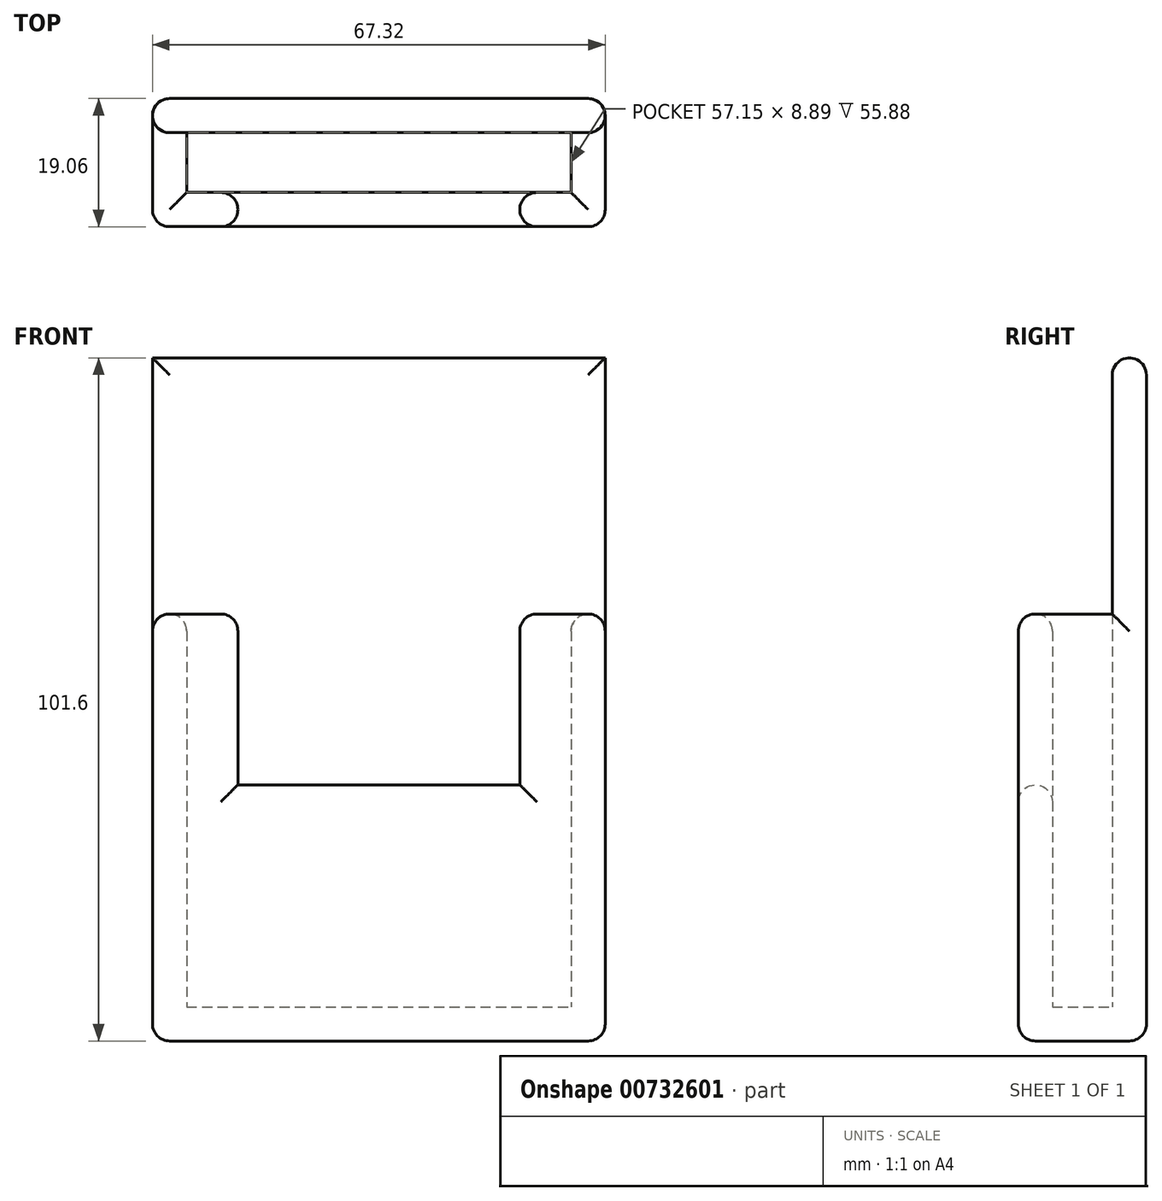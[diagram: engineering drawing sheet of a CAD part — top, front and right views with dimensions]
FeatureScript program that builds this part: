
annotation { "Feature Type Name" : "Feature", "Feature Type Description" : "" }
export const myFeature = defineFeature(function(context is Context, id is Id, definition is map)
    precondition{}
    {
        {
            var Q0;
            Q0=qCreatedBy(makeId("Top.planeOp"),FACE);
            var sketch = newSketch(context, id + "F0", { "sketchPlane" : qUnion([Q0])});
            skLineSegment(sketch, "E0.bottom", {"start": v(-33.66, 9.53) * mm, "end": v(33.66, 9.53) * mm});
            skLineSegment(sketch, "E0.top", {"start": v(-33.66, -9.53) * mm, "end": v(33.66, -9.53) * mm});
            skLineSegment(sketch, "E0.left", {"start": v(-33.66, 9.53) * mm, "end": v(-33.66, -9.53) * mm});
            skLineSegment(sketch, "E0.right", {"start": v(33.66, 9.53) * mm, "end": v(33.66, -9.53) * mm});
            skPoint(sketch, "E0.middle", {"position": v(0, 0) * mm});
            skLineSegment(sketch, "E1.0", {"start": v(-28.58, 4.45) * mm, "end": v(28.58, 4.45) * mm});
            skLineSegment(sketch, "E1.1", {"start": v(-28.58, 4.45) * mm, "end": v(-28.58, -4.45) * mm});
            skLineSegment(sketch, "E1.2", {"start": v(-28.58, -4.45) * mm, "end": v(28.58, -4.45) * mm});
            skLineSegment(sketch, "E1.3", {"start": v(28.58, 4.44) * mm, "end": v(28.58, -4.45) * mm});
            skLineSegment(sketch, "E2", {"start": v(-20.96, -4.45) * mm, "end": v(-20.96, -9.53) * mm});
            skLineSegment(sketch, "E3", {"start": v(20.96, -4.45) * mm, "end": v(20.96, -9.53) * mm});
            skLineSegment(sketch, "E4", {"start": v(-28.58, 4.45) * mm, "end": v(-33.66, 4.45) * mm});
            skLineSegment(sketch, "E5", {"start": v(28.58, 4.44) * mm, "end": v(33.66, 4.44) * mm});
            skSolve(sketch);
        }
        {
            var Q0;
            Q0 = qSketchRegion(id + "F0", true);
            var Q1;
            Q1=makeQuery(id+"F0.imprint","IMPRINT",FACE,{"disambiguationData":[TD([[makeQuery(id+"F0.imprint","IMPRINT",EDGE,{"derivedFrom":sQuery(id+"F0.wireOp",EDGE,"E1.0")}),-1.0]])]});
            extrude(context, id + "F1", {"entities" : qUnion([Q0, Q1]), "depth" : 5.08 * mm, "offsetDistance" : 25.4 * mm});
        }
        {
            var Q0;
            {var subQ1=sQuery(id+"F0.wireOp",EDGE,"E0.bottom");Q0=makeQuery(id+"F0.imprint","IMPRINT",FACE,{"disambiguationData":[TD([[makeQuery(id+"F0.imprint","IMPRINT",EDGE,{"derivedFrom":subQ1}),-1.0]])]});}
            extrude(context, id + "F2", {"entities" : qUnion([Q0]), "operationType" : NewBodyOperationType.ADD, "depth" : 101.6 * mm, "offsetDistance" : 25.4 * mm});
        }
        {
            var Q0;
            {var subQ0=sQuery(id+"F0.wireOp",EDGE,"E1.1");Q0=makeQuery(id+"F0.imprint","IMPRINT",FACE,{"disambiguationData":[TD([[makeQuery(id+"F0.imprint","IMPRINT",EDGE,{"derivedFrom":subQ0}),-1.0]])]});}
            var Q1;
            {var subQ0=sQuery(id+"F0.wireOp",EDGE,"E1.3");Q1=makeQuery(id+"F0.imprint","IMPRINT",FACE,{"disambiguationData":[TD([[makeQuery(id+"F0.imprint","IMPRINT",EDGE,{"derivedFrom":subQ0}),1.0]])]});}
            extrude(context, id + "F3", {"entities" : qUnion([Q0, Q1]), "operationType" : NewBodyOperationType.ADD, "depth" : 63.5 * mm, "offsetDistance" : 25.4 * mm});
        }
        {
            var Q0;
            {var subQ0=sQuery(id+"F0.wireOp",EDGE,"E2");Q0=makeQuery(id+"F0.imprint","IMPRINT",FACE,{"disambiguationData":[TD([[makeQuery(id+"F0.imprint","IMPRINT",EDGE,{"derivedFrom":subQ0}),1.0]])]});}
            extrude(context, id + "F4", {"entities" : qUnion([Q0]), "operationType" : NewBodyOperationType.ADD, "depth" : 38.1 * mm, "offsetDistance" : 25.4 * mm});
        }
        {
            var Q0;
            Q0=makeQuery(id+"F2.opExtrude","SWEPT_EDGE",EDGE,{"disambiguationData":[OSD([sQuery(id+"F0.wireOp",EDGE,"E0.left"),sQuery(id+"F0.wireOp",EDGE,"E4")])]});
            var Q1;
            {var subQ0=sQuery(id+"F0.wireOp",EDGE,"E0.right");var subQ1=sQuery(id+"F0.wireOp",EDGE,"E0.bottom");Q1=makeQuery(id+"F2.boolean.opBoolean","MERGE",EDGE,{"derivedFrom":[makeQuery(id+"F1.opExtrude","SWEPT_EDGE",EDGE,{"disambiguationData":[OSD([subQ1,subQ0])]}),makeQuery(id+"F2.opExtrude","SWEPT_EDGE",EDGE,{"disambiguationData":[OSD([subQ1,subQ0])]})]});}
            var Q2;
            Q2=makeQuery(id+"F2.opExtrude","SWEPT_EDGE",EDGE,{"disambiguationData":[OSD([sQuery(id+"F0.wireOp",EDGE,"E0.right"),sQuery(id+"F0.wireOp",EDGE,"E5")])]});
            var Q3;
            Q3=makeQuery(id+"F2.opExtrude","CAP_EDGE",EDGE,{"disambiguationData":[OSD([sQuery(id+"F0.wireOp",EDGE,"E1.0"),sQuery(id+"F0.wireOp",EDGE,"E4"),sQuery(id+"F0.wireOp",EDGE,"E5")])],"isStart":false});
            var Q4;
            Q4=makeQuery(id+"F2.opExtrude","CAP_EDGE",EDGE,{"disambiguationData":[OSD([sQuery(id+"F0.wireOp",EDGE,"E0.bottom")])],"isStart":false});
            var Q5;
            {var subQ0=sQuery(id+"F0.wireOp",EDGE,"E0.left");var subQ1=sQuery(id+"F0.wireOp",EDGE,"E0.bottom");Q5=makeQuery(id+"F2.boolean.opBoolean","MERGE",EDGE,{"derivedFrom":[makeQuery(id+"F1.opExtrude","SWEPT_EDGE",EDGE,{"disambiguationData":[OSD([subQ1,subQ0])]}),makeQuery(id+"F2.opExtrude","SWEPT_EDGE",EDGE,{"disambiguationData":[OSD([subQ1,subQ0])]})]});}
            var Q6;
            Q6=makeQuery(id+"F1.opExtrude","CAP_EDGE",EDGE,{"disambiguationData":[OSD([sQuery(id+"F0.wireOp",EDGE,"E0.bottom")])],"isStart":true});
            var Q7;
            Q7=makeQuery(id+"F3.opExtrude","CAP_EDGE",EDGE,{"disambiguationData":[OSD([sQuery(id+"F0.wireOp",EDGE,"E0.right")])],"isStart":false});
            var Q8;
            {var subQ0=sQuery(id+"F0.wireOp",EDGE,"E1.2");Q8=makeQuery(id+"F3.opExtrude","CAP_EDGE",EDGE,{"disambiguationData":[OSD([subQ0]),TDD([makeQuery(id+"F0.imprint","IMPRINT",EDGE,{"disambiguationData":[TD([[makeQuery(id+"F0.imprint","INTERSECT",VERTEX,{"derivedFrom":[subQ0,sQuery(id+"F0.wireOp",EDGE,"E1.3")]}),1.0]])],"derivedFrom":subQ0})])],"isStart":false});}
            var Q9;
            Q9=makeQuery(id+"F3.opExtrude","CAP_EDGE",EDGE,{"disambiguationData":[OSD([sQuery(id+"F0.wireOp",EDGE,"E1.3")])],"isStart":false});
            var Q10;
            {var subQ0=sQuery(id+"F0.wireOp",EDGE,"E0.top");Q10=makeQuery(id+"F3.opExtrude","CAP_EDGE",EDGE,{"disambiguationData":[OSD([subQ0]),TDD([makeQuery(id+"F0.imprint","IMPRINT",EDGE,{"disambiguationData":[TD([[makeQuery(id+"F0.imprint","INTERSECT",VERTEX,{"derivedFrom":[subQ0,sQuery(id+"F0.wireOp",EDGE,"E0.right")]}),1.0]])],"derivedFrom":subQ0})])],"isStart":false});}
            var Q11;
            Q11=makeQuery(id+"F3.opExtrude","CAP_EDGE",EDGE,{"disambiguationData":[OSD([sQuery(id+"F0.wireOp",EDGE,"E3")])],"isStart":false});
            var Q12;
            {var subQ0=sQuery(id+"F0.wireOp",EDGE,"E0.right");var subQ1=sQuery(id+"F0.wireOp",EDGE,"E0.top");Q12=makeQuery(id+"F3.boolean.opBoolean","MERGE",EDGE,{"derivedFrom":[makeQuery(id+"F1.opExtrude","SWEPT_EDGE",EDGE,{"disambiguationData":[OSD([subQ1,subQ0])]}),makeQuery(id+"F3.opExtrude","SWEPT_EDGE",EDGE,{"disambiguationData":[OSD([subQ1,subQ0])]})]});}
            var Q13;
            Q13=makeQuery(id+"F3.opExtrude","SWEPT_EDGE",EDGE,{"disambiguationData":[OSD([sQuery(id+"F0.wireOp",EDGE,"E0.top"),sQuery(id+"F0.wireOp",EDGE,"E3")])]});
            var Q14;
            Q14=makeQuery(id+"F4.opExtrude","CAP_EDGE",EDGE,{"disambiguationData":[OSD([sQuery(id+"F0.wireOp",EDGE,"E0.top")])],"isStart":false});
            var Q15;
            Q15=makeQuery(id+"F3.opExtrude","SWEPT_EDGE",EDGE,{"disambiguationData":[OSD([sQuery(id+"F0.wireOp",EDGE,"E0.top"),sQuery(id+"F0.wireOp",EDGE,"E2")])]});
            var Q16;
            Q16=makeQuery(id+"F3.opExtrude","SWEPT_EDGE",EDGE,{"disambiguationData":[OSD([sQuery(id+"F0.wireOp",EDGE,"E1.2"),sQuery(id+"F0.wireOp",EDGE,"E2")])]});
            var Q17;
            {var subQ0=sQuery(id+"F0.wireOp",EDGE,"E0.top");Q17=makeQuery(id+"F3.opExtrude","CAP_EDGE",EDGE,{"disambiguationData":[OSD([subQ0]),TDD([makeQuery(id+"F0.imprint","IMPRINT",EDGE,{"disambiguationData":[TD([[makeQuery(id+"F0.imprint","INTERSECT",VERTEX,{"derivedFrom":[subQ0,sQuery(id+"F0.wireOp",EDGE,"E0.left")]}),-1.0]])],"derivedFrom":subQ0})])],"isStart":false});}
            var Q18;
            {var subQ0=sQuery(id+"F0.wireOp",EDGE,"E1.2");Q18=makeQuery(id+"F3.opExtrude","CAP_EDGE",EDGE,{"disambiguationData":[OSD([subQ0]),TDD([makeQuery(id+"F0.imprint","IMPRINT",EDGE,{"disambiguationData":[TD([[makeQuery(id+"F0.imprint","INTERSECT",VERTEX,{"derivedFrom":[sQuery(id+"F0.wireOp",EDGE,"E1.1"),subQ0]}),-1.0]])],"derivedFrom":subQ0})])],"isStart":false});}
            var Q19;
            Q19=makeQuery(id+"F3.opExtrude","CAP_EDGE",EDGE,{"disambiguationData":[OSD([sQuery(id+"F0.wireOp",EDGE,"E1.1")])],"isStart":false});
            var Q20;
            Q20=makeQuery(id+"F3.opExtrude","CAP_EDGE",EDGE,{"disambiguationData":[OSD([sQuery(id+"F0.wireOp",EDGE,"E0.left")])],"isStart":false});
            var Q21;
            {var subQ0=sQuery(id+"F0.wireOp",EDGE,"E0.left");var subQ1=sQuery(id+"F0.wireOp",EDGE,"E0.top");Q21=makeQuery(id+"F3.boolean.opBoolean","MERGE",EDGE,{"derivedFrom":[makeQuery(id+"F1.opExtrude","SWEPT_EDGE",EDGE,{"disambiguationData":[OSD([subQ1,subQ0])]}),makeQuery(id+"F3.opExtrude","SWEPT_EDGE",EDGE,{"disambiguationData":[OSD([subQ1,subQ0])]})]});}
            var Q22;
            Q22=makeQuery(id+"F1.opExtrude","CAP_EDGE",EDGE,{"disambiguationData":[OSD([sQuery(id+"F0.wireOp",EDGE,"E0.top")])],"isStart":true});
            var Q23;
            Q23=makeQuery(id+"F1.opExtrude","CAP_EDGE",EDGE,{"disambiguationData":[OSD([sQuery(id+"F0.wireOp",EDGE,"E0.right")])],"isStart":true});
            var Q24;
            Q24=makeQuery(id+"F1.opExtrude","CAP_EDGE",EDGE,{"disambiguationData":[OSD([sQuery(id+"F0.wireOp",EDGE,"E0.left")])],"isStart":true});
            var Q25;
            Q25=makeQuery(id+"F3.opExtrude","CAP_EDGE",EDGE,{"disambiguationData":[OSD([sQuery(id+"F0.wireOp",EDGE,"E2")])],"isStart":false});
            var Q26;
            Q26=makeQuery(id+"F4.opExtrude","CAP_EDGE",EDGE,{"disambiguationData":[OSD([sQuery(id+"F0.wireOp",EDGE,"E1.2")])],"isStart":false});
            var Q27;
            Q27=makeQuery(id+"F3.opExtrude","SWEPT_EDGE",EDGE,{"disambiguationData":[OSD([sQuery(id+"F0.wireOp",EDGE,"E1.2"),sQuery(id+"F0.wireOp",EDGE,"E3")])]});
            fillet(context, id + "F5", {"entities" : qUnion([Q0, Q1, Q2, Q3, Q4, Q5, Q6, Q7, Q8, Q9, Q10, Q11, Q12, Q13, Q14, Q15, Q16, Q17, Q18, Q19, Q20, Q21, Q22, Q23, Q24, Q25, Q26, Q27]), "radius" : 2.54 * mm, "tangentPropagation" : true, "allowEdgeOverflow" : false});
        }
    });
